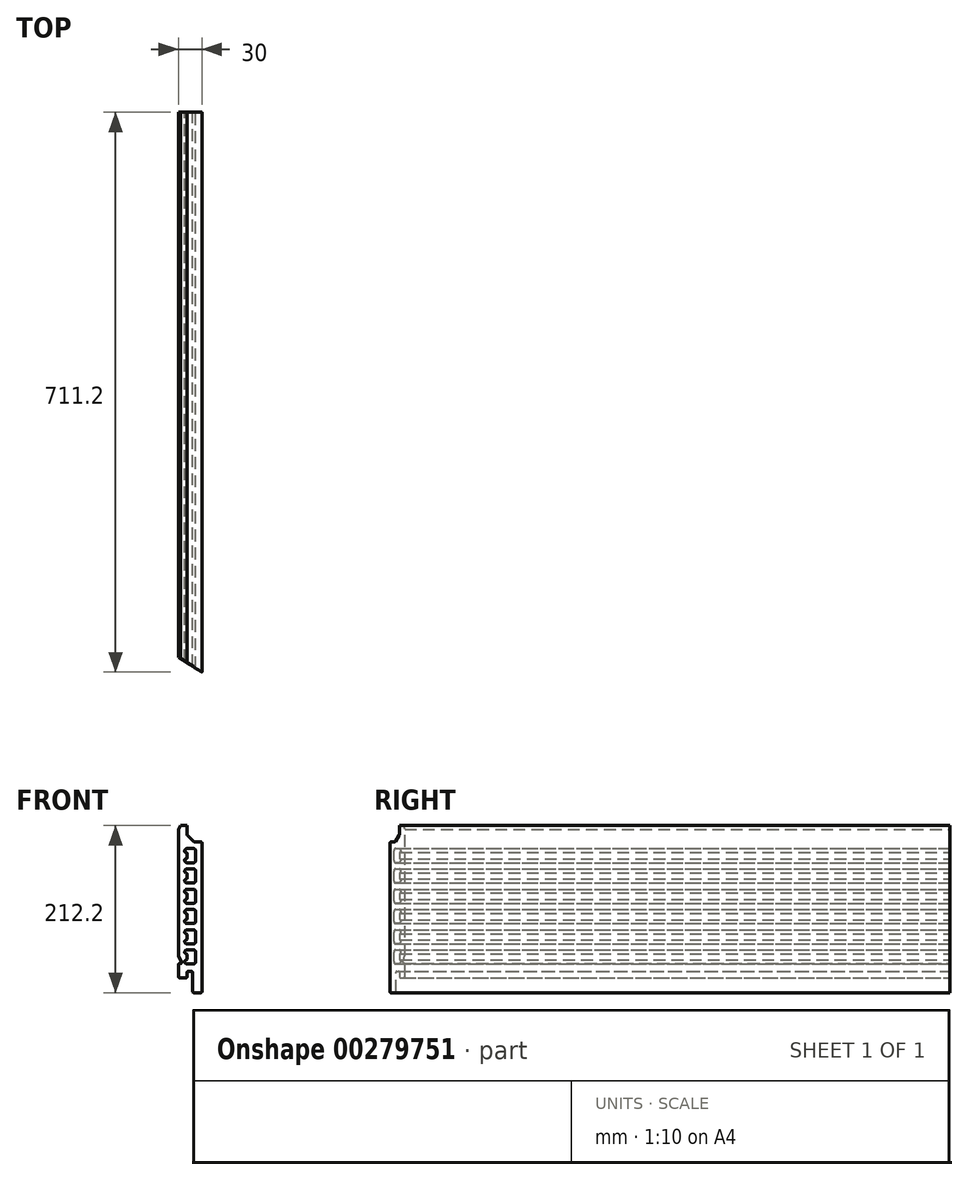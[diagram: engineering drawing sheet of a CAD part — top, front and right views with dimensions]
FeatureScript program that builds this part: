
annotation { "Feature Type Name" : "Feature", "Feature Type Description" : "" }
export const myFeature = defineFeature(function(context is Context, id is Id, definition is map)
    precondition{}
    {
        {
            var Q0;
            Q0=qCreatedBy(makeId("Front.planeOp"),FACE);
            var sketch = newSketch(context, id + "F0", { "sketchPlane" : qUnion([Q0])});
            skLineSegment(sketch, "E0", {"start": v(-14.86, -59.63) * mm, "end": v(-11.1, -67.7) * mm});
            skArc(sketch, "E1", {"start": v(-11.1, -67.7) * mm, "mid": v(-11.16, -68.66) * mm, "end": v(-12, -69.12) * mm});
            skLineSegment(sketch, "E2", {"start": v(-12, -69.12) * mm, "end": v(-14, -69.12) * mm});
            skArc(sketch, "E3", {"start": v(-14, -69.12) * mm, "mid": v(-14.7, -69.41) * mm, "end": v(-15, -70.12) * mm});
            skLineSegment(sketch, "E4", {"start": v(-15, -70.12) * mm, "end": v(-15, -85.6) * mm});
            skArc(sketch, "E5", {"start": v(-15, -85.6) * mm, "mid": v(-14.56, -86.66) * mm, "end": v(-13.5, -87.1) * mm});
            skLineSegment(sketch, "E6", {"start": v(-13.5, -87.1) * mm, "end": v(-5.5, -87.1) * mm});
            skArc(sketch, "E7", {"start": v(-5.5, -87.1) * mm, "mid": v(-4.44, -86.66) * mm, "end": v(-4, -85.6) * mm});
            skLineSegment(sketch, "E8", {"start": v(-4, -85.6) * mm, "end": v(-4, -80.6) * mm});
            skArc(sketch, "E9", {"start": v(-4, -80.6) * mm, "mid": v(-3.56, -79.54) * mm, "end": v(-2.5, -79.1) * mm});
            skLineSegment(sketch, "E10", {"start": v(-2.5, -79.1) * mm, "end": v(1.48, -79.1) * mm});
            skArc(sketch, "E11", {"start": v(1.48, -79.1) * mm, "mid": v(2.54, -79.54) * mm, "end": v(2.98, -80.6) * mm});
            skLineSegment(sketch, "E12", {"start": v(2.98, -80.6) * mm, "end": v(2.98, -104.6) * mm});
            skArc(sketch, "E13", {"start": v(2.98, -104.6) * mm, "mid": v(3.42, -105.66) * mm, "end": v(4.48, -106.1) * mm});
            skLineSegment(sketch, "E14", {"start": v(4.48, -106.1) * mm, "end": v(13.5, -106.1) * mm});
            skArc(sketch, "E15", {"start": v(13.5, -106.1) * mm, "mid": v(14.56, -105.66) * mm, "end": v(15, -104.6) * mm});
            skLineSegment(sketch, "E16", {"start": v(15, -104.6) * mm, "end": v(15, 83.78) * mm});
            skArc(sketch, "E17", {"start": v(15, 83.78) * mm, "mid": v(14.58, 84.81) * mm, "end": v(13.57, 85.27) * mm});
            skLineSegment(sketch, "E18", {"start": v(13.57, 85.27) * mm, "end": v(5.1, 85.66) * mm});
            skArc(sketch, "E19", {"start": v(5.1, 85.66) * mm, "mid": v(4.57, 85.79) * mm, "end": v(4.11, 86.1) * mm});
            skLineSegment(sketch, "E20", {"start": v(4.11, 86.1) * mm, "end": v(-3.56, 93.77) * mm});
            skArc(sketch, "E21", {"start": v(-3.56, 93.77) * mm, "mid": v(-3.89, 94.26) * mm, "end": v(-4, 94.83) * mm});
            skLineSegment(sketch, "E22", {"start": v(-4, 94.83) * mm, "end": v(-4, 106.1) * mm});
            skLineSegment(sketch, "E23", {"start": v(-4, 106.1) * mm, "end": v(-12.31, 106.1) * mm});
            skLineSegment(sketch, "E24", {"start": v(-12.31, 106.1) * mm, "end": v(-15, 101.2) * mm});
            skLineSegment(sketch, "E25", {"start": v(-15, 101.2) * mm, "end": v(-15, -59) * mm});
            skArc(sketch, "E26", {"start": v(-15, -59) * mm, "mid": v(-14.96, -59.32) * mm, "end": v(-14.86, -59.63) * mm});
            skArc(sketch, "E27", {"start": v(-14.86, -59.63) * mm, "mid": v(-14.96, -59.32) * mm, "end": v(-15, -59) * mm});
            skSolve(sketch);
        }
        {
            var Q0;
            Q0=makeQuery(id+"F0.imprint","IMPRINT",FACE,{"disambiguationData":[TD([[makeQuery(id+"F0.imprint","IMPRINT",EDGE,{"derivedFrom":sQuery(id+"F0.wireOp",EDGE,"E3")}),1.0]])]});
            extrude(context, id + "F1", {"entities" : qUnion([Q0]), "depth" : 711.2 * mm});
        }
        {
            var Q0;
            Q0=qCreatedBy(makeId("Front.planeOp"),FACE);
            var sketch = newSketch(context, id + "F2", { "sketchPlane" : qUnion([Q0])});
            skArc(sketch, "E28", {"start": v(-4, -32.7) * mm, "mid": v(-4.43, -31.63) * mm, "end": v(-5.5, -31.2) * mm});
            skLineSegment(sketch, "E29", {"start": v(-5.5, -31.2) * mm, "end": v(-5.5, -31.2) * mm});
            skArc(sketch, "E30", {"start": v(-5.5, -31.2) * mm, "mid": v(-6.56, -30.76) * mm, "end": v(-7, -29.7) * mm});
            skLineSegment(sketch, "E31", {"start": v(-7, -29.7) * mm, "end": v(-7, -29.2) * mm});
            skArc(sketch, "E32", {"start": v(-7, -29.2) * mm, "mid": v(-6.12, -27.07) * mm, "end": v(-4, -26.2) * mm});
            skLineSegment(sketch, "E33", {"start": v(-4, -26.2) * mm, "end": v(4, -26.2) * mm});
            skArc(sketch, "E34", {"start": v(4, -26.2) * mm, "mid": v(6.12, -27.07) * mm, "end": v(7, -29.2) * mm});
            skLineSegment(sketch, "E35", {"start": v(7, -29.2) * mm, "end": v(7, -41.2) * mm});
            skArc(sketch, "E36", {"start": v(7, -41.2) * mm, "mid": v(6.12, -43.32) * mm, "end": v(4, -44.2) * mm});
            skLineSegment(sketch, "E37", {"start": v(4, -44.2) * mm, "end": v(-4, -44.2) * mm});
            skArc(sketch, "E38", {"start": v(-4, -44.2) * mm, "mid": v(-6.12, -43.32) * mm, "end": v(-7, -41.2) * mm});
            skLineSegment(sketch, "E39", {"start": v(-7, -41.2) * mm, "end": v(-7, -40.7) * mm});
            skArc(sketch, "E40", {"start": v(-7, -40.7) * mm, "mid": v(-6.56, -39.63) * mm, "end": v(-5.5, -39.2) * mm});
            skLineSegment(sketch, "E41", {"start": v(-5.5, -39.2) * mm, "end": v(-5.5, -39.2) * mm});
            skArc(sketch, "E42", {"start": v(-5.5, -39.2) * mm, "mid": v(-4.43, -38.76) * mm, "end": v(-4, -37.7) * mm});
            skLineSegment(sketch, "E43", {"start": v(-4, -37.7) * mm, "end": v(-4, -32.7) * mm});
            skArc(sketch, "E44", {"start": v(-4, -58.1) * mm, "mid": v(-4.43, -57.03) * mm, "end": v(-5.5, -56.6) * mm});
            skLineSegment(sketch, "E45", {"start": v(-5.5, -56.6) * mm, "end": v(-5.5, -56.6) * mm});
            skArc(sketch, "E46", {"start": v(-5.5, -56.6) * mm, "mid": v(-6.56, -56.16) * mm, "end": v(-7, -55.1) * mm});
            skLineSegment(sketch, "E47", {"start": v(-7, -55.1) * mm, "end": v(-7, -54.6) * mm});
            skArc(sketch, "E48", {"start": v(-7, -54.6) * mm, "mid": v(-6.12, -52.47) * mm, "end": v(-4, -51.6) * mm});
            skLineSegment(sketch, "E49", {"start": v(-4, -51.6) * mm, "end": v(4, -51.6) * mm});
            skArc(sketch, "E50", {"start": v(4, -51.6) * mm, "mid": v(6.12, -52.47) * mm, "end": v(7, -54.6) * mm});
            skLineSegment(sketch, "E51", {"start": v(7, -54.6) * mm, "end": v(7, -66.6) * mm});
            skArc(sketch, "E52", {"start": v(7, -66.6) * mm, "mid": v(6.12, -68.72) * mm, "end": v(4, -69.6) * mm});
            skLineSegment(sketch, "E53", {"start": v(4, -69.6) * mm, "end": v(-4, -69.6) * mm});
            skArc(sketch, "E54", {"start": v(-4, -69.6) * mm, "mid": v(-6.12, -68.72) * mm, "end": v(-7, -66.6) * mm});
            skLineSegment(sketch, "E55", {"start": v(-7, -66.6) * mm, "end": v(-7, -66.1) * mm});
            skArc(sketch, "E56", {"start": v(-7, -66.1) * mm, "mid": v(-6.56, -65.03) * mm, "end": v(-5.5, -64.6) * mm});
            skLineSegment(sketch, "E57", {"start": v(-5.5, -64.6) * mm, "end": v(-5.5, -64.6) * mm});
            skArc(sketch, "E58", {"start": v(-5.5, -64.6) * mm, "mid": v(-4.43, -64.16) * mm, "end": v(-4, -63.1) * mm});
            skLineSegment(sketch, "E59", {"start": v(-4, -63.1) * mm, "end": v(-4, -58.1) * mm});
            skArc(sketch, "E60", {"start": v(-4, -6.9) * mm, "mid": v(-4.43, -5.83) * mm, "end": v(-5.5, -5.4) * mm});
            skLineSegment(sketch, "E61", {"start": v(-5.5, -5.4) * mm, "end": v(-5.5, -5.4) * mm});
            skArc(sketch, "E62", {"start": v(-5.5, -5.4) * mm, "mid": v(-6.56, -4.96) * mm, "end": v(-7, -3.9) * mm});
            skLineSegment(sketch, "E63", {"start": v(-7, -3.9) * mm, "end": v(-7, -3.4) * mm});
            skArc(sketch, "E64", {"start": v(-7, -3.4) * mm, "mid": v(-6.12, -1.27) * mm, "end": v(-4, -0.4) * mm});
            skLineSegment(sketch, "E65", {"start": v(-4, -0.4) * mm, "end": v(4, -0.4) * mm});
            skArc(sketch, "E66", {"start": v(4, -0.4) * mm, "mid": v(6.12, -1.27) * mm, "end": v(7, -3.4) * mm});
            skLineSegment(sketch, "E67", {"start": v(7, -3.4) * mm, "end": v(7, -15.4) * mm});
            skArc(sketch, "E68", {"start": v(7, -15.4) * mm, "mid": v(6.12, -17.52) * mm, "end": v(4, -18.4) * mm});
            skLineSegment(sketch, "E69", {"start": v(4, -18.4) * mm, "end": v(-4, -18.4) * mm});
            skArc(sketch, "E70", {"start": v(-4, -18.4) * mm, "mid": v(-6.12, -17.52) * mm, "end": v(-7, -15.4) * mm});
            skLineSegment(sketch, "E71", {"start": v(-7, -15.4) * mm, "end": v(-7, -14.9) * mm});
            skArc(sketch, "E72", {"start": v(-7, -14.9) * mm, "mid": v(-6.56, -13.83) * mm, "end": v(-5.5, -13.4) * mm});
            skLineSegment(sketch, "E73", {"start": v(-5.5, -13.4) * mm, "end": v(-5.5, -13.4) * mm});
            skArc(sketch, "E74", {"start": v(-5.5, -13.4) * mm, "mid": v(-4.43, -12.96) * mm, "end": v(-4, -11.9) * mm});
            skLineSegment(sketch, "E75", {"start": v(-4, -11.9) * mm, "end": v(-4, -6.9) * mm});
            skLineSegment(sketch, "E76", {"start": v(-5.5, 20.4) * mm, "end": v(-5.5, 20.4) * mm});
            skArc(sketch, "E77", {"start": v(-5.5, 20.4) * mm, "mid": v(-6.56, 20.84) * mm, "end": v(-7, 21.9) * mm});
            skLineSegment(sketch, "E78", {"start": v(-7, 21.9) * mm, "end": v(-7, 22.4) * mm});
            skArc(sketch, "E79", {"start": v(-7, 22.4) * mm, "mid": v(-6.12, 24.52) * mm, "end": v(-4, 25.4) * mm});
            skLineSegment(sketch, "E80", {"start": v(-4, 25.4) * mm, "end": v(4, 25.4) * mm});
            skArc(sketch, "E81", {"start": v(4, 25.4) * mm, "mid": v(6.12, 24.52) * mm, "end": v(7, 22.4) * mm});
            skLineSegment(sketch, "E82", {"start": v(7, 22.4) * mm, "end": v(7, 10.4) * mm});
            skArc(sketch, "E83", {"start": v(7, 10.4) * mm, "mid": v(6.12, 8.28) * mm, "end": v(4, 7.4) * mm});
            skLineSegment(sketch, "E84", {"start": v(4, 7.4) * mm, "end": v(-4, 7.4) * mm});
            skArc(sketch, "E85", {"start": v(-4, 7.4) * mm, "mid": v(-6.12, 8.28) * mm, "end": v(-7, 10.4) * mm});
            skLineSegment(sketch, "E86", {"start": v(-7, 10.4) * mm, "end": v(-7, 10.9) * mm});
            skArc(sketch, "E87", {"start": v(-7, 10.9) * mm, "mid": v(-6.56, 11.96) * mm, "end": v(-5.5, 12.4) * mm});
            skLineSegment(sketch, "E88", {"start": v(-5.5, 12.4) * mm, "end": v(-5.5, 12.4) * mm});
            skArc(sketch, "E89", {"start": v(-5.5, 12.4) * mm, "mid": v(-4.43, 12.84) * mm, "end": v(-4, 13.9) * mm});
            skLineSegment(sketch, "E90", {"start": v(-4, 13.9) * mm, "end": v(-4, 18.9) * mm});
            skArc(sketch, "E91", {"start": v(-4, 18.9) * mm, "mid": v(-4.43, 19.96) * mm, "end": v(-5.5, 20.4) * mm});
            skLineSegment(sketch, "E92", {"start": v(-5.5, 46.2) * mm, "end": v(-5.5, 46.2) * mm});
            skArc(sketch, "E93", {"start": v(-5.5, 46.2) * mm, "mid": v(-6.56, 46.64) * mm, "end": v(-7, 47.7) * mm});
            skLineSegment(sketch, "E94", {"start": v(-7, 47.7) * mm, "end": v(-7, 48.2) * mm});
            skArc(sketch, "E95", {"start": v(-7, 48.2) * mm, "mid": v(-6.12, 50.32) * mm, "end": v(-4, 51.2) * mm});
            skLineSegment(sketch, "E96", {"start": v(-4, 51.2) * mm, "end": v(4, 51.2) * mm});
            skArc(sketch, "E97", {"start": v(4, 51.2) * mm, "mid": v(6.12, 50.32) * mm, "end": v(7, 48.2) * mm});
            skLineSegment(sketch, "E98", {"start": v(7, 48.2) * mm, "end": v(7, 36.2) * mm});
            skArc(sketch, "E99", {"start": v(7, 36.2) * mm, "mid": v(6.12, 34.08) * mm, "end": v(4, 33.2) * mm});
            skLineSegment(sketch, "E100", {"start": v(4, 33.2) * mm, "end": v(-4, 33.2) * mm});
            skArc(sketch, "E101", {"start": v(-4, 33.2) * mm, "mid": v(-6.12, 34.08) * mm, "end": v(-7, 36.2) * mm});
            skLineSegment(sketch, "E102", {"start": v(-7, 36.2) * mm, "end": v(-7, 36.7) * mm});
            skArc(sketch, "E103", {"start": v(-7, 36.7) * mm, "mid": v(-6.56, 37.76) * mm, "end": v(-5.5, 38.2) * mm});
            skLineSegment(sketch, "E104", {"start": v(-5.5, 38.2) * mm, "end": v(-5.5, 38.2) * mm});
            skArc(sketch, "E105", {"start": v(-5.5, 38.2) * mm, "mid": v(-4.43, 38.64) * mm, "end": v(-4, 39.7) * mm});
            skLineSegment(sketch, "E106", {"start": v(-4, 39.7) * mm, "end": v(-4, 44.7) * mm});
            skArc(sketch, "E107", {"start": v(-4, 44.7) * mm, "mid": v(-4.43, 45.76) * mm, "end": v(-5.5, 46.2) * mm});
            skLineSegment(sketch, "E108", {"start": v(-5.5, 72) * mm, "end": v(-5.5, 72) * mm});
            skArc(sketch, "E109", {"start": v(-5.5, 72) * mm, "mid": v(-6.56, 72.43) * mm, "end": v(-7, 73.5) * mm});
            skLineSegment(sketch, "E110", {"start": v(-7, 73.5) * mm, "end": v(-7, 74) * mm});
            skArc(sketch, "E111", {"start": v(-7, 74) * mm, "mid": v(-6.12, 76.12) * mm, "end": v(-4, 77) * mm});
            skLineSegment(sketch, "E112", {"start": v(-4, 77) * mm, "end": v(4, 77) * mm});
            skArc(sketch, "E113", {"start": v(4, 77) * mm, "mid": v(6.12, 76.12) * mm, "end": v(7, 74) * mm});
            skLineSegment(sketch, "E114", {"start": v(7, 74) * mm, "end": v(7, 62) * mm});
            skArc(sketch, "E115", {"start": v(7, 62) * mm, "mid": v(6.12, 59.87) * mm, "end": v(4, 59) * mm});
            skLineSegment(sketch, "E116", {"start": v(4, 59) * mm, "end": v(-4, 59) * mm});
            skArc(sketch, "E117", {"start": v(-4, 59) * mm, "mid": v(-6.12, 59.87) * mm, "end": v(-7, 62) * mm});
            skLineSegment(sketch, "E118", {"start": v(-7, 62) * mm, "end": v(-7, 62.5) * mm});
            skArc(sketch, "E119", {"start": v(-7, 62.5) * mm, "mid": v(-6.56, 63.56) * mm, "end": v(-5.5, 64) * mm});
            skLineSegment(sketch, "E120", {"start": v(-5.5, 64) * mm, "end": v(-5.5, 64) * mm});
            skArc(sketch, "E121", {"start": v(-5.5, 64) * mm, "mid": v(-4.43, 64.43) * mm, "end": v(-4, 65.5) * mm});
            skLineSegment(sketch, "E122", {"start": v(-4, 65.5) * mm, "end": v(-4, 70.5) * mm});
            skArc(sketch, "E123", {"start": v(-4, 70.5) * mm, "mid": v(-4.43, 71.56) * mm, "end": v(-5.5, 72) * mm});
            skLineSegment(sketch, "E124", {"start": v(0, -69.6) * mm, "end": v(-0.5, -77) * mm});
            skSolve(sketch);
        }
        {
            var Q0;
            Q0=qSketchRegion(id+"F2",true);
            extrude(context, id + "F3", {"entities" : qUnion([Q0]), "operationType" : NewBodyOperationType.REMOVE, "depth" : 711.2 * mm});
        }
        {
            var Q0;
            Q0=qCreatedBy(makeId("Top.planeOp"),FACE);
            var sketch = newSketch(context, id + "F4", { "sketchPlane" : qUnion([Q0])});
            skLineSegment(sketch, "E125", {"start": v(15.12, -711.27) * mm, "end": v(-15.04, -711.27) * mm});
            skLineSegment(sketch, "E126", {"start": v(-15.04, -711.27) * mm, "end": v(-15.04, -692.22) * mm});
            skLineSegment(sketch, "E127", {"start": v(-15.04, -692.22) * mm, "end": v(15.12, -711.27) * mm});
            skSolve(sketch);
        }
        {
            var Q0;
            Q0 = qSketchRegion(id + "F4", true);
            extrude(context, id + "F5", {"entities" : qUnion([Q0]), "operationType" : NewBodyOperationType.REMOVE, "endBound" : BoundingType.THROUGH_ALL, "depth" : 25.4 * mm, "hasSecondDirection" : true, "secondDirectionBound" : SecondDirectionBoundingType.THROUGH_ALL, "secondDirectionOppositeDirection" : true, "secondDirectionDepth" : 25.4 * mm});
        }
    });
